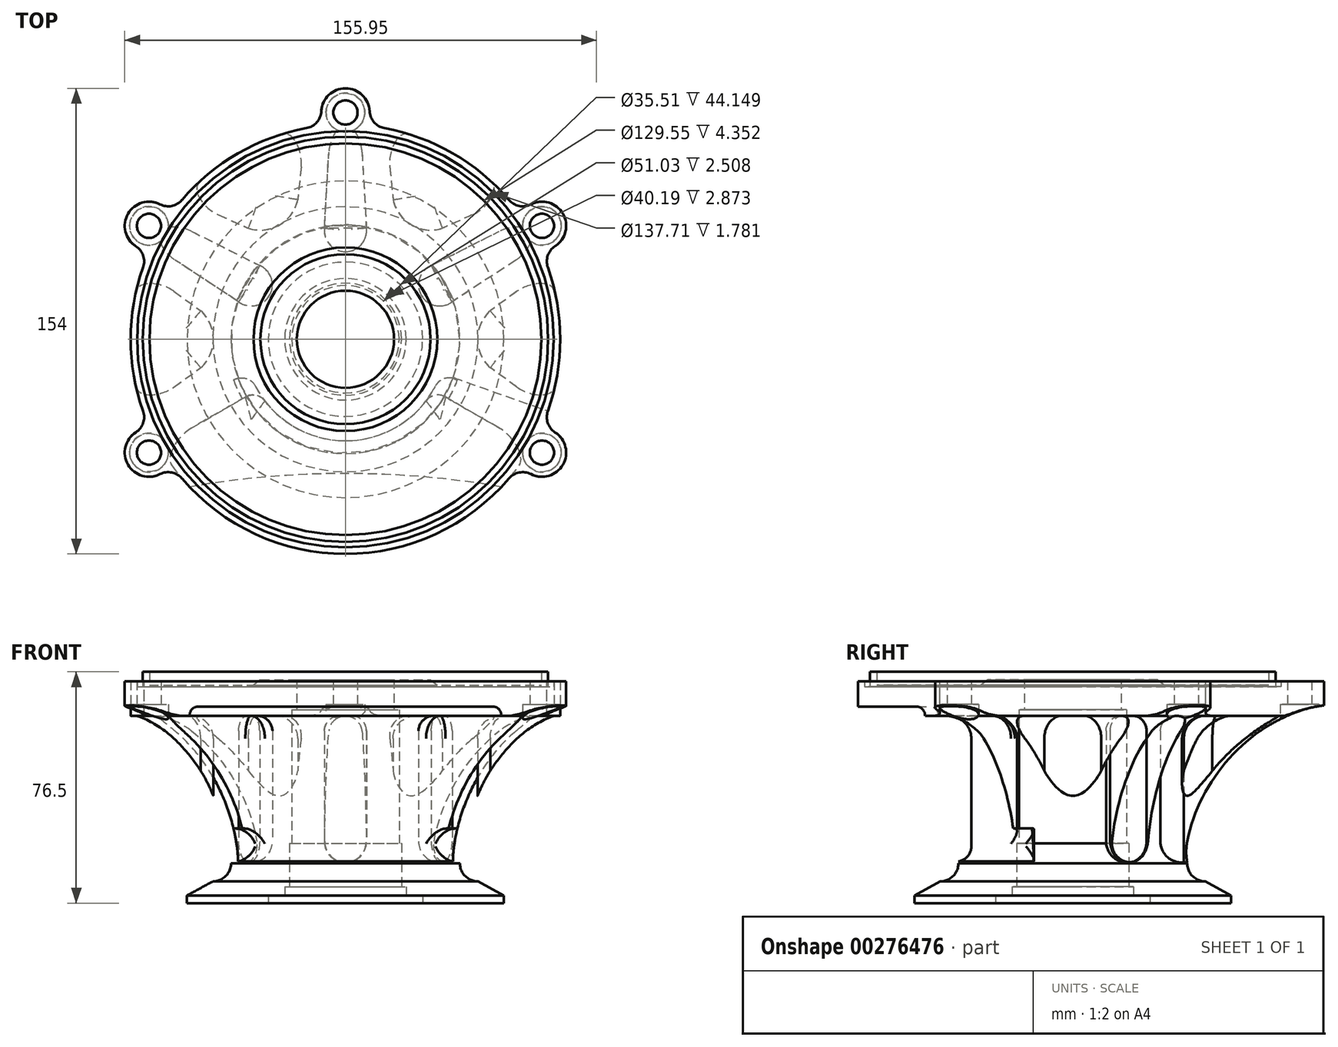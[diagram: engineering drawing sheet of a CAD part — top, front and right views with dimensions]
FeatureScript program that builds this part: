
annotation { "Feature Type Name" : "Feature", "Feature Type Description" : "" }
export const myFeature = defineFeature(function(context is Context, id is Id, definition is map)
    precondition{}
    {
        {
            var Q0;
            Q0=qCreatedBy(makeId("Top.planeOp"),FACE);
            var sketch = newSketch(context, id + "F0", { "sketchPlane" : qUnion([Q0])});
            skCircle(sketch, "E0", {"center": v(0, 0) * mm, "radius": 71 * mm});
            skLineSegment(sketch, "E1", {"start": v(0, 75) * mm, "end": v(0, -75) * mm, "construction": true});
            skCircle(sketch, "E2", {"center": v(0, 0) * mm, "radius": 15 * mm});
            skLineSegment(sketch, "E3", {"start": v(-75, 0) * mm, "end": v(75, 0) * mm, "construction": true});
            skLineSegment(sketch, "E4", {"start": v(-64.95, -37.5) * mm, "end": v(64.95, 37.5) * mm, "construction": true});
            skLineSegment(sketch, "E5.MirrorCS", {"start": v(64.95, -37.5) * mm, "end": v(-64.95, 37.5) * mm, "construction": true});
            skCircle(sketch, "E6", {"center": v(0, 75) * mm, "radius": 4 * mm});
            skCircle(sketch, "E7", {"center": v(-64.95, 37.5) * mm, "radius": 4 * mm});
            skCircle(sketch, "E8", {"center": v(64.95, 37.5) * mm, "radius": 4 * mm});
            skCircle(sketch, "E9", {"center": v(0, 75) * mm, "radius": 8 * mm});
            skCircle(sketch, "E10", {"center": v(64.95, 37.5) * mm, "radius": 8 * mm});
            skCircle(sketch, "E11", {"center": v(-64.95, 37.5) * mm, "radius": 8 * mm});
            skCircle(sketch, "E12", {"center": v(-64.95, -37.5) * mm, "radius": 4 * mm});
            skCircle(sketch, "E13", {"center": v(-64.95, -37.5) * mm, "radius": 8 * mm});
            skCircle(sketch, "E14", {"center": v(64.95, -37.5) * mm, "radius": 4 * mm});
            skCircle(sketch, "E15", {"center": v(64.95, -37.5) * mm, "radius": 8 * mm});
            skSolve(sketch);
        }
        {
            var Q0;
            Q0 = qSketchRegion(id + "F0", true);
            extrude(context, id + "F1", {"entities" : qUnion([Q0]), "depth" : 76.5 * mm});
        }
        {
            var Q0;
            {var subQ0=sQuery(id+"F0.wireOp",EDGE,"Xowyf9vp-Wtrz-lmeA-m8cz-GKDCjoLcK8KI");var subQ1=sQuery(id+"F0.wireOp",EDGE,"E0");Q0=makeQuery(id+"F1.opExtrude","SWEPT_EDGE",EDGE,{"disambiguationData":[OSD([subQ1,subQ0]),TDD([makeQuery(id+"F0.imprint","INTERSECT",VERTEX,{"disambiguationData":[OD(1.0)],"derivedFrom":[subQ1,subQ0]})])]});}
            var Q1;
            {var subQ0=sQuery(id+"F0.wireOp",EDGE,"Xowyf9vp-Wtrz-lmeA-m8cz-GKDCjoLcK8KI");var subQ1=sQuery(id+"F0.wireOp",EDGE,"E0");Q1=makeQuery(id+"F1.opExtrude","SWEPT_EDGE",EDGE,{"disambiguationData":[OSD([subQ1,subQ0]),TDD([makeQuery(id+"F0.imprint","INTERSECT",VERTEX,{"disambiguationData":[OD(0.0)],"derivedFrom":[subQ1,subQ0]})])]});}
            var Q2;
            {var subQ0=sQuery(id+"F0.wireOp",EDGE,"E11");var subQ1=sQuery(id+"F0.wireOp",EDGE,"E0");Q2=makeQuery(id+"F1.opExtrude","SWEPT_EDGE",EDGE,{"disambiguationData":[OSD([subQ1,subQ0]),TDD([makeQuery(id+"F0.imprint","INTERSECT",VERTEX,{"disambiguationData":[OD(0.0)],"derivedFrom":[subQ1,subQ0]})])]});}
            var Q3;
            {var subQ0=sQuery(id+"F0.wireOp",EDGE,"E11");var subQ1=sQuery(id+"F0.wireOp",EDGE,"E0");Q3=makeQuery(id+"F1.opExtrude","SWEPT_EDGE",EDGE,{"disambiguationData":[OSD([subQ1,subQ0]),TDD([makeQuery(id+"F0.imprint","INTERSECT",VERTEX,{"disambiguationData":[OD(1.0)],"derivedFrom":[subQ1,subQ0]})])]});}
            var Q4;
            {var subQ0=sQuery(id+"F0.wireOp",EDGE,"E9");var subQ1=sQuery(id+"F0.wireOp",EDGE,"E0");Q4=makeQuery(id+"F1.opExtrude","SWEPT_EDGE",EDGE,{"disambiguationData":[OSD([subQ1,subQ0]),TDD([makeQuery(id+"F0.imprint","INTERSECT",VERTEX,{"disambiguationData":[OD(1.0)],"derivedFrom":[subQ1,subQ0]})])]});}
            var Q5;
            {var subQ0=sQuery(id+"F0.wireOp",EDGE,"E9");var subQ1=sQuery(id+"F0.wireOp",EDGE,"E0");Q5=makeQuery(id+"F1.opExtrude","SWEPT_EDGE",EDGE,{"disambiguationData":[OSD([subQ1,subQ0]),TDD([makeQuery(id+"F0.imprint","INTERSECT",VERTEX,{"disambiguationData":[OD(0.0)],"derivedFrom":[subQ1,subQ0]})])]});}
            var Q6;
            {var subQ0=sQuery(id+"F0.wireOp",EDGE,"E10");var subQ1=sQuery(id+"F0.wireOp",EDGE,"E0");Q6=makeQuery(id+"F1.opExtrude","SWEPT_EDGE",EDGE,{"disambiguationData":[OSD([subQ1,subQ0]),TDD([makeQuery(id+"F0.imprint","INTERSECT",VERTEX,{"disambiguationData":[OD(1.0)],"derivedFrom":[subQ1,subQ0]})])]});}
            var Q7;
            {var subQ0=sQuery(id+"F0.wireOp",EDGE,"E10");var subQ1=sQuery(id+"F0.wireOp",EDGE,"E0");Q7=makeQuery(id+"F1.opExtrude","SWEPT_EDGE",EDGE,{"disambiguationData":[OSD([subQ1,subQ0]),TDD([makeQuery(id+"F0.imprint","INTERSECT",VERTEX,{"disambiguationData":[OD(0.0)],"derivedFrom":[subQ1,subQ0]})])]});}
            var Q8;
            {var subQ0=sQuery(id+"F0.wireOp",EDGE,"yhjaQ4TD-eABU-w7vi-KoSL-NEqgUzHXku1N");var subQ1=sQuery(id+"F0.wireOp",EDGE,"E0");Q8=makeQuery(id+"F1.opExtrude","SWEPT_EDGE",EDGE,{"disambiguationData":[OSD([subQ1,subQ0]),TDD([makeQuery(id+"F0.imprint","INTERSECT",VERTEX,{"disambiguationData":[OD(0.0)],"derivedFrom":[subQ1,subQ0]})])]});}
            var Q9;
            {var subQ0=sQuery(id+"F0.wireOp",EDGE,"yhjaQ4TD-eABU-w7vi-KoSL-NEqgUzHXku1N");var subQ1=sQuery(id+"F0.wireOp",EDGE,"E0");Q9=makeQuery(id+"F1.opExtrude","SWEPT_EDGE",EDGE,{"disambiguationData":[OSD([subQ1,subQ0]),TDD([makeQuery(id+"F0.imprint","INTERSECT",VERTEX,{"disambiguationData":[OD(1.0)],"derivedFrom":[subQ1,subQ0]})])]});}
            var Q10;
            {var subQ0=sQuery(id+"F0.wireOp",EDGE,"E13");var subQ1=sQuery(id+"F0.wireOp",EDGE,"E0");Q10=makeQuery(id+"F1.opExtrude","SWEPT_EDGE",EDGE,{"disambiguationData":[OSD([subQ1,subQ0]),TDD([makeQuery(id+"F0.imprint","INTERSECT",VERTEX,{"disambiguationData":[OD(0.0)],"derivedFrom":[subQ1,subQ0]})])]});}
            var Q11;
            {var subQ0=sQuery(id+"F0.wireOp",EDGE,"E13");var subQ1=sQuery(id+"F0.wireOp",EDGE,"E0");Q11=makeQuery(id+"F1.opExtrude","SWEPT_EDGE",EDGE,{"disambiguationData":[OSD([subQ1,subQ0]),TDD([makeQuery(id+"F0.imprint","INTERSECT",VERTEX,{"disambiguationData":[OD(1.0)],"derivedFrom":[subQ1,subQ0]})])]});}
            var Q12;
            {var subQ0=sQuery(id+"F0.wireOp",EDGE,"E15");var subQ1=sQuery(id+"F0.wireOp",EDGE,"E0");Q12=makeQuery(id+"F1.opExtrude","SWEPT_EDGE",EDGE,{"disambiguationData":[OSD([subQ1,subQ0]),TDD([makeQuery(id+"F0.imprint","INTERSECT",VERTEX,{"disambiguationData":[OD(0.0)],"derivedFrom":[subQ1,subQ0]})])]});}
            var Q13;
            {var subQ0=sQuery(id+"F0.wireOp",EDGE,"E15");var subQ1=sQuery(id+"F0.wireOp",EDGE,"E0");Q13=makeQuery(id+"F1.opExtrude","SWEPT_EDGE",EDGE,{"disambiguationData":[OSD([subQ1,subQ0]),TDD([makeQuery(id+"F0.imprint","INTERSECT",VERTEX,{"disambiguationData":[OD(1.0)],"derivedFrom":[subQ1,subQ0]})])]});}
            fillet(context, id + "F2", {"entities" : qUnion([Q0, Q1, Q2, Q3, Q4, Q5, Q6, Q7, Q8, Q9, Q10, Q11, Q12, Q13]), "radius" : 6 * mm, "tangentPropagation" : true, "allowEdgeOverflow" : false});
        }
        {
            var Q0;
            Q0=qCreatedBy(makeId("Front.planeOp"),FACE);
            var sketch = newSketch(context, id + "F3", { "sketchPlane" : qUnion([Q0])});
            skLineSegment(sketch, "E16", {"start": v(0, 91.9) * mm, "end": v(98, 91.9) * mm});
            skLineSegment(sketch, "E17", {"start": v(0, 91.9) * mm, "end": v(0, 0) * mm});
            skLineSegment(sketch, "E18", {"start": v(0, 0) * mm, "end": v(0, -15.6) * mm});
            skLineSegment(sketch, "E19", {"start": v(98, 91.9) * mm, "end": v(98, 73.4) * mm});
            skLineSegment(sketch, "E20", {"start": v(98, 73.4) * mm, "end": v(68.85, 73.4) * mm});
            skLineSegment(sketch, "E21", {"start": v(68.85, 73.4) * mm, "end": v(68.85, 71.6) * mm});
            skLineSegment(sketch, "E22", {"start": v(68.85, 71.6) * mm, "end": v(67, 71.6) * mm});
            skLineSegment(sketch, "E23", {"start": v(67, 71.6) * mm, "end": v(67, 76.5) * mm});
            skLineSegment(sketch, "E24", {"start": v(67, 76.5) * mm, "end": v(64.78, 76.5) * mm});
            skLineSegment(sketch, "E25", {"start": v(64.78, 76.5) * mm, "end": v(64.78, 72.15) * mm});
            skLineSegment(sketch, "E26", {"start": v(64.78, 72.15) * mm, "end": v(30.38, 72.15) * mm});
            skLineSegment(sketch, "E27", {"start": v(28.11, 73.9) * mm, "end": v(16.06, 73.9) * mm});
            skLineSegment(sketch, "E28", {"start": v(16.06, 73.9) * mm, "end": v(16.06, 63.9) * mm});
            skLineSegment(sketch, "E29", {"start": v(16.06, 63.9) * mm, "end": v(17.76, 63.9) * mm});
            skLineSegment(sketch, "E30", {"start": v(0, -15.6) * mm, "end": v(98, -15.6) * mm});
            skLineSegment(sketch, "E31", {"start": v(98, -15.6) * mm, "end": v(98, 65.9) * mm});
            skLineSegment(sketch, "E32", {"start": v(17.76, 63.9) * mm, "end": v(17.76, 19.75) * mm});
            skLineSegment(sketch, "E33", {"start": v(17.76, 19.75) * mm, "end": v(18.54, 19.75) * mm});
            skLineSegment(sketch, "E34", {"start": v(18.54, 19.75) * mm, "end": v(18.54, 5.38) * mm});
            skLineSegment(sketch, "E35", {"start": v(18.54, 5.38) * mm, "end": v(20.1, 5.38) * mm});
            skLineSegment(sketch, "E36", {"start": v(20.1, 5.38) * mm, "end": v(20.1, 2.5) * mm});
            skLineSegment(sketch, "E37", {"start": v(20.1, 2.5) * mm, "end": v(25.52, 2.5) * mm});
            skLineSegment(sketch, "E38", {"start": v(25.52, 2.5) * mm, "end": v(25.52, 0) * mm});
            skLineSegment(sketch, "E39", {"start": v(25.52, 0) * mm, "end": v(52.38, 0) * mm});
            skLineSegment(sketch, "E40", {"start": v(52.38, 0) * mm, "end": v(52.38, 2.5) * mm});
            skLineSegment(sketch, "E41", {"start": v(52.38, 2.5) * mm, "end": v(43.83, 7.18) * mm});
            skLineSegment(sketch, "E42", {"start": v(43.83, 7.18) * mm, "end": v(43.81, 7.18) * mm});
            skLineSegment(sketch, "E43", {"start": v(98, 65.9) * mm, "end": v(87.97, 65.9) * mm});
            skPoint(sketch, "E44.visualSharp", {"position": v(37.81, 7.18) * mm});
            skArc(sketch, "E44.filletArc", {"start": v(37.81, 13.18) * mm, "mid": v(39.57, 8.94) * mm, "end": v(43.81, 7.18) * mm});
            skFitSpline(sketch, "E45", {"points": [v(37.81, 13.18) * mm, v(87.97, 65.9) * mm], "startDerivative": vector(-0.87, 63.39) * mm, "endDerivative": vector(91.68, 3.94) * mm});
            skLineSegment(sketch, "E46", {"start": v(25.52, 0) * mm, "end": v(0, 0) * mm, "construction": true});
            skLineSegment(sketch, "E47", {"start": v(28.11, 73.9) * mm, "end": v(30.38, 72.15) * mm});
            skSolve(sketch);
        }
        {
            var Q0;
            Q0 = qSketchRegion(id + "F3", true);
            var Q1;
            Q1=sQuery(id+"F3.wireOp",EDGE,"E17");
            revolve(context, id + "F4", {"operationType" : NewBodyOperationType.REMOVE, "entities" : qUnion([Q0]), "axis" : qUnion([Q1]), "revolveType" : RevolveType.FULL, "oppositeDirection" : true});
        }
        {
            var Q0;
            Q0=qCreatedBy(makeId("Top.planeOp"),FACE);
            var sketch = newSketch(context, id + "F5", { "sketchPlane" : qUnion([Q0])});
            skCircle(sketch, "E48", {"center": v(0, 0) * mm, "radius": 43.67 * mm, "construction": true});
            skLineSegment(sketch, "E49", {"start": v(88.93, -51.34) * mm, "end": v(-88.93, 51.34) * mm, "construction": true});
            skLineSegment(sketch, "E50", {"start": v(-118.94, 0) * mm, "end": v(121.39, 0) * mm, "construction": true});
            skLineSegment(sketch, "E51", {"start": v(0, -76.85) * mm, "end": v(0, 108.09) * mm, "construction": true});
            skLineSegment(sketch, "E52.MirrorCS", {"start": v(-88.93, -51.34) * mm, "end": v(88.93, 51.34) * mm, "construction": true});
            skArc(sketch, "E53", {"start": v(4.56, 78.17) * mm, "mid": v(0, 82.73) * mm, "end": v(-4.56, 78.17) * mm});
            skArc(sketch, "E54", {"start": v(-6.93, 36.75) * mm, "mid": v(0, 28.98) * mm, "end": v(6.93, 36.75) * mm});
            skLineSegment(sketch, "E55", {"start": v(-6.98, 35.95) * mm, "end": v(6.98, 35.95) * mm, "construction": true});
            skLineSegment(sketch, "E56", {"start": v(-4.56, 78.17) * mm, "end": v(4.56, 78.17) * mm, "construction": true});
            skLineSegment(sketch, "E57", {"start": v(4.56, 78.17) * mm, "end": v(6.98, 35.95) * mm});
            skLineSegment(sketch, "E58", {"start": v(-6.98, 35.95) * mm, "end": v(-4.56, 78.17) * mm});
            skArc(sketch, "E59.1.0", {"start": v(28.36, 24.38) * mm, "mid": v(25.1, 14.49) * mm, "end": v(35.3, 12.37) * mm});
            skLineSegment(sketch, "E59.1.1", {"start": v(27.65, 24.02) * mm, "end": v(65.42, 43.03) * mm});
            skLineSegment(sketch, "E59.1.2", {"start": v(69.98, 35.14) * mm, "end": v(34.63, 11.93) * mm});
            skArc(sketch, "E59.1.3", {"start": v(69.98, 35.14) * mm, "mid": v(71.65, 41.36) * mm, "end": v(65.42, 43.03) * mm});
            skLineSegment(sketch, "E59.anchor1", {"start": v(0, 0) * mm, "end": v(-6.93, 36.75) * mm, "construction": true});
            skLineSegment(sketch, "E59.anchor2", {"start": v(0, 0) * mm, "end": v(28.36, 24.38) * mm, "construction": true});
            skLineSegment(sketch, "E60.anchor2", {"start": v(0, 0) * mm, "end": v(6.93, -36.75) * mm, "construction": true});
            skLineSegment(sketch, "E61.1.0", {"start": v(-65.42, 43.03) * mm, "end": v(-27.65, 24.02) * mm});
            skArc(sketch, "E61.1.1", {"start": v(-65.42, 43.03) * mm, "mid": v(-71.65, 41.36) * mm, "end": v(-69.98, 35.14) * mm});
            skLineSegment(sketch, "E61.1.2", {"start": v(-34.63, 11.93) * mm, "end": v(-69.98, 35.14) * mm});
            skArc(sketch, "E61.1.3", {"start": v(-35.3, 12.37) * mm, "mid": v(-25.1, 14.49) * mm, "end": v(-28.36, 24.38) * mm});
            skLineSegment(sketch, "E61.anchor1", {"start": v(0, 0) * mm, "end": v(-4.56, -78.17) * mm, "construction": true});
            skLineSegment(sketch, "E61.anchor2", {"start": v(0, 0) * mm, "end": v(-65.42, 43.03) * mm, "construction": true});
            skArc(sketch, "E62", {"start": v(-101.6, 0) * mm, "mid": v(-90.55, -20.82) * mm, "end": v(-67.1, -23.33) * mm});
            skLineSegment(sketch, "E63", {"start": v(-67.1, -23.33) * mm, "end": v(-47.84, -9.43) * mm});
            skArc(sketch, "E64.trimOffspring", {"start": v(-47.84, -9.43) * mm, "mid": v(-44.76, -5.15) * mm, "end": v(-43.67, 0) * mm});
            skArc(sketch, "E65.MirrorCS", {"start": v(-101.6, 0) * mm, "mid": v(-90.55, 20.82) * mm, "end": v(-67.1, 23.33) * mm});
            skLineSegment(sketch, "E66.MirrorCS", {"start": v(-67.1, 23.33) * mm, "end": v(-47.84, 9.43) * mm});
            skArc(sketch, "E67.MirrorCS", {"start": v(-47.84, 9.43) * mm, "mid": v(-44.76, 5.15) * mm, "end": v(-43.67, 0) * mm});
            skArc(sketch, "E68.1.0", {"start": v(-50.8, 88) * mm, "mid": v(-63.3, 68) * mm, "end": v(-53.76, 46.45) * mm});
            skLineSegment(sketch, "E68.1.1", {"start": v(-53.76, 46.45) * mm, "end": v(-32.08, 36.71) * mm});
            skArc(sketch, "E68.1.2", {"start": v(-32.08, 36.71) * mm, "mid": v(-26.84, 36.18) * mm, "end": v(-21.83, 37.82) * mm});
            skArc(sketch, "E68.1.3", {"start": v(-15.75, 46.14) * mm, "mid": v(-17.92, 41.34) * mm, "end": v(-21.83, 37.82) * mm});
            skLineSegment(sketch, "E68.1.4", {"start": v(-13.35, 69.78) * mm, "end": v(-15.75, 46.14) * mm});
            skArc(sketch, "E68.1.5", {"start": v(-50.8, 88) * mm, "mid": v(-27.24, 88.83) * mm, "end": v(-13.35, 69.78) * mm});
            skArc(sketch, "E68.2.0", {"start": v(50.8, 88) * mm, "mid": v(27.24, 88.83) * mm, "end": v(13.35, 69.78) * mm});
            skLineSegment(sketch, "E68.2.1", {"start": v(13.35, 69.78) * mm, "end": v(15.75, 46.14) * mm});
            skArc(sketch, "E68.2.2", {"start": v(15.75, 46.14) * mm, "mid": v(17.92, 41.34) * mm, "end": v(21.83, 37.82) * mm});
            skArc(sketch, "E68.2.3", {"start": v(32.08, 36.71) * mm, "mid": v(26.84, 36.18) * mm, "end": v(21.83, 37.82) * mm});
            skLineSegment(sketch, "E68.2.4", {"start": v(53.76, 46.45) * mm, "end": v(32.08, 36.71) * mm});
            skArc(sketch, "E68.2.5", {"start": v(50.8, 88) * mm, "mid": v(63.3, 68) * mm, "end": v(53.76, 46.45) * mm});
            skArc(sketch, "E68.3.0", {"start": v(101.6, 0) * mm, "mid": v(90.55, 20.82) * mm, "end": v(67.1, 23.33) * mm});
            skLineSegment(sketch, "E68.3.1", {"start": v(67.1, 23.33) * mm, "end": v(47.84, 9.43) * mm});
            skArc(sketch, "E68.3.2", {"start": v(47.84, 9.43) * mm, "mid": v(44.76, 5.15) * mm, "end": v(43.67, 0) * mm});
            skArc(sketch, "E68.3.3", {"start": v(47.84, -9.43) * mm, "mid": v(44.76, -5.15) * mm, "end": v(43.67, 0) * mm});
            skLineSegment(sketch, "E68.3.4", {"start": v(67.1, -23.33) * mm, "end": v(47.84, -9.43) * mm});
            skArc(sketch, "E68.3.5", {"start": v(101.6, 0) * mm, "mid": v(90.55, -20.82) * mm, "end": v(67.1, -23.33) * mm});
            skLineSegment(sketch, "E68.anchor1", {"start": v(0, 0) * mm, "end": v(-101.6, 0) * mm, "construction": true});
            skLineSegment(sketch, "E68.anchor2", {"start": v(0, 0) * mm, "end": v(101.6, 0) * mm, "construction": true});
            skCircle(sketch, "E69.0", {"center": v(-64.95, -37.5) * mm, "radius": 4 * mm});
            skCircle(sketch, "E70.0", {"center": v(64.95, -37.5) * mm, "radius": 4 * mm});
            skLineSegment(sketch, "E71", {"start": v(-64.95, -37.5) * mm, "end": v(-29.05, -16.77) * mm});
            skLineSegment(sketch, "E72", {"start": v(64.95, -37.5) * mm, "end": v(29.05, -16.77) * mm});
            skArc(sketch, "E73", {"start": v(-63.86, -47.91) * mm, "mid": v(0, -79.83) * mm, "end": v(63.86, -47.91) * mm});
            skArc(sketch, "E74", {"start": v(63.86, -47.91) * mm, "mid": v(65.4, -41.07) * mm, "end": v(61.3, -35.4) * mm});
            skArc(sketch, "E75.MirrorC", {"start": v(-63.86, -47.91) * mm, "mid": v(-65.4, -41.07) * mm, "end": v(-61.3, -35.4) * mm});
            skArc(sketch, "E76.trimOffspring", {"start": v(-29.05, -16.77) * mm, "mid": v(0, -33.55) * mm, "end": v(29.05, -16.77) * mm});
            skArc(sketch, "E77.trimOffspring", {"start": v(-6.22, 32.97) * mm, "mid": v(-6.26, 32.96) * mm, "end": v(-6.3, 32.95) * mm});
            skArc(sketch, "E78.trimOffspring", {"start": v(25.44, 21.87) * mm, "mid": v(25.41, 21.9) * mm, "end": v(25.39, 21.93) * mm});
            skSolve(sketch);
        }
        {
            var Q0;
            Q0 = qSketchRegion(id + "F5", true);
            extrude(context, id + "F6", {"entities" : qUnion([Q0]), "operationType" : NewBodyOperationType.REMOVE, "depth" : 61.94 * mm, "hasSecondDirection" : true, "secondDirectionOppositeDirection" : false, "secondDirectionDepth" : 20.4 * mm});
        }
        {
            var Q0;
            Q0=makeQuery(id+"F6.boolean.opBoolean","COPY",FACE,{"derivedFrom":makeQuery(id+"F6.opExtrude","CAP_FACE",FACE,{"disambiguationData":[OSD([sQuery(id+"F5.wireOp",EDGE,"E59.1.0"),sQuery(id+"F5.wireOp",EDGE,"E59.1.1"),sQuery(id+"F5.wireOp",EDGE,"E59.1.2"),sQuery(id+"F5.wireOp",EDGE,"E59.1.3")])],"isStart":true})});
            var sketch = newSketch(context, id + "F7", { "sketchPlane" : qUnion([Q0])});
            skLineSegment(sketch, "E79.0.0", {"start": v(29.31, 24.86) * mm, "end": v(28.36, 24.38) * mm});
            skArc(sketch, "E79.0.1", {"start": v(28.36, 24.38) * mm, "mid": v(25.1, 14.49) * mm, "end": v(35.3, 12.37) * mm});
            skLineSegment(sketch, "E79.0.2", {"start": v(35.3, 12.37) * mm, "end": v(36.18, 12.96) * mm});
            skArc(sketch, "E79.0.3", {"start": v(36.18, 12.96) * mm, "mid": v(33.28, 19.22) * mm, "end": v(29.31, 24.86) * mm});
            skLineSegment(sketch, "E80", {"start": v(31.14, 17.98) * mm, "end": v(33.28, 19.22) * mm});
            skLineSegment(sketch, "E81", {"start": v(33.28, 19.22) * mm, "end": v(25.1, 14.49) * mm});
            skSolve(sketch);
        }
        {
            var Q0;
            {var subQ1=sQuery(id+"F7.wireOp",EDGE,"E79.0.0");Q0=makeQuery(id+"F7.imprint","IMPRINT",FACE,{"disambiguationData":[TD([[makeQuery(id+"F7.imprint","IMPRINT",EDGE,{"derivedFrom":subQ1}),-1.0]])]});}
            var Q1;
            Q1=sQuery(id+"F7.wireOp",EDGE,"E81");
            revolve(context, id + "F8", {"operationType" : NewBodyOperationType.REMOVE, "entities" : qUnion([Q0]), "axis" : qUnion([Q1]), "revolveType" : RevolveType.FULL, "oppositeDirection" : true});
        }
        {
            var Q0;
            Q0=makeQuery(id+"F6.boolean.opBoolean","COPY",FACE,{"derivedFrom":makeQuery(id+"F6.opExtrude","CAP_FACE",FACE,{"disambiguationData":[OSD([sQuery(id+"F5.wireOp",EDGE,"E53"),sQuery(id+"F5.wireOp",EDGE,"E54"),sQuery(id+"F5.wireOp",EDGE,"E57"),sQuery(id+"F5.wireOp",EDGE,"E58")])],"isStart":true})});
            var sketch = newSketch(context, id + "F9", { "sketchPlane" : qUnion([Q0])});
            skLineSegment(sketch, "E82.0.0", {"start": v(-6.87, 37.81) * mm, "end": v(-6.93, 36.75) * mm});
            skArc(sketch, "E82.0.1", {"start": v(-6.93, 36.75) * mm, "mid": v(0, 28.98) * mm, "end": v(6.93, 36.75) * mm});
            skLineSegment(sketch, "E82.0.2", {"start": v(6.93, 36.75) * mm, "end": v(6.87, 37.81) * mm});
            skArc(sketch, "E82.0.3", {"start": v(6.87, 37.81) * mm, "mid": v(0, 38.43) * mm, "end": v(-6.87, 37.81) * mm});
            skLineSegment(sketch, "E83", {"start": v(0, 28.98) * mm, "end": v(0, 38.43) * mm});
            skSolve(sketch);
        }
        {
            var Q0;
            {var subQ0=sQuery(id+"F9.wireOp",EDGE,"E82.0.0");Q0=makeQuery(id+"F9.imprint","IMPRINT",FACE,{"disambiguationData":[TD([[makeQuery(id+"F9.imprint","IMPRINT",EDGE,{"derivedFrom":subQ0}),-1.0]])]});}
            var Q1;
            Q1=sQuery(id+"F9.wireOp",EDGE,"E83");
            revolve(context, id + "F10", {"operationType" : NewBodyOperationType.REMOVE, "entities" : qUnion([Q0]), "axis" : qUnion([Q1]), "revolveType" : RevolveType.FULL, "oppositeDirection" : true});
        }
        {
            var Q0;
            Q0=makeQuery(id+"F6.boolean.opBoolean","COPY",FACE,{"derivedFrom":makeQuery(id+"F6.opExtrude","CAP_FACE",FACE,{"disambiguationData":[OSD([sQuery(id+"F5.wireOp",EDGE,"E61.1.0"),sQuery(id+"F5.wireOp",EDGE,"E61.1.1"),sQuery(id+"F5.wireOp",EDGE,"E61.1.2"),sQuery(id+"F5.wireOp",EDGE,"E61.1.3")])],"isStart":true})});
            var sketch = newSketch(context, id + "F11", { "sketchPlane" : qUnion([Q0])});
            skLineSegment(sketch, "E84.0.0", {"start": v(-36.18, 12.96) * mm, "end": v(-35.3, 12.37) * mm});
            skArc(sketch, "E84.0.1", {"start": v(-35.3, 12.37) * mm, "mid": v(-25.1, 14.49) * mm, "end": v(-28.36, 24.38) * mm});
            skLineSegment(sketch, "E84.0.2", {"start": v(-28.36, 24.38) * mm, "end": v(-29.31, 24.86) * mm});
            skArc(sketch, "E84.0.3", {"start": v(-29.31, 24.86) * mm, "mid": v(-33.28, 19.22) * mm, "end": v(-36.18, 12.96) * mm});
            skLineSegment(sketch, "E85", {"start": v(-25.1, 14.49) * mm, "end": v(-33.28, 19.22) * mm});
            skSolve(sketch);
        }
        {
            var Q0;
            {var subQ0=sQuery(id+"F11.wireOp",EDGE,"E84.0.0");Q0=makeQuery(id+"F11.imprint","IMPRINT",FACE,{"disambiguationData":[TD([[makeQuery(id+"F11.imprint","IMPRINT",EDGE,{"derivedFrom":subQ0}),-1.0]])]});}
            var Q1;
            Q1=sQuery(id+"F11.wireOp",EDGE,"E85");
            revolve(context, id + "F12", {"operationType" : NewBodyOperationType.REMOVE, "entities" : qUnion([Q0]), "axis" : qUnion([Q1]), "revolveType" : RevolveType.FULL, "oppositeDirection" : true});
        }
        {
            var Q0;
            Q0=makeQuery(id+"F6.boolean.opBoolean","COPY",EDGE,{"derivedFrom":makeQuery(id+"F6.opExtrude","CAP_EDGE",EDGE,{"disambiguationData":[OSD([sQuery(id+"F5.wireOp",EDGE,"E68.1.2"),sQuery(id+"F5.wireOp",EDGE,"E68.1.3")])],"isStart":false})});
            var Q1;
            Q1=makeQuery(id+"F6.boolean.opBoolean","COPY",EDGE,{"derivedFrom":makeQuery(id+"F6.opExtrude","CAP_EDGE",EDGE,{"disambiguationData":[OSD([sQuery(id+"F5.wireOp",EDGE,"E68.1.1")])],"isStart":false})});
            var Q2;
            Q2=makeQuery(id+"F6.boolean.opBoolean","COPY",EDGE,{"derivedFrom":makeQuery(id+"F6.opExtrude","CAP_EDGE",EDGE,{"disambiguationData":[OSD([sQuery(id+"F5.wireOp",EDGE,"E68.1.4")])],"isStart":false})});
            var Q3;
            Q3=makeQuery(id+"F6.boolean.opBoolean","COPY",EDGE,{"derivedFrom":makeQuery(id+"F6.opExtrude","CAP_EDGE",EDGE,{"disambiguationData":[OSD([sQuery(id+"F5.wireOp",EDGE,"E68.2.1")])],"isStart":false})});
            var Q4;
            Q4=makeQuery(id+"F6.boolean.opBoolean","COPY",EDGE,{"derivedFrom":makeQuery(id+"F6.opExtrude","CAP_EDGE",EDGE,{"disambiguationData":[OSD([sQuery(id+"F5.wireOp",EDGE,"E68.2.2"),sQuery(id+"F5.wireOp",EDGE,"E68.2.3")])],"isStart":false})});
            var Q5;
            Q5=makeQuery(id+"F6.boolean.opBoolean","COPY",EDGE,{"derivedFrom":makeQuery(id+"F6.opExtrude","CAP_EDGE",EDGE,{"disambiguationData":[OSD([sQuery(id+"F5.wireOp",EDGE,"E68.2.4")])],"isStart":false})});
            var Q6;
            Q6=makeQuery(id+"F6.boolean.opBoolean","COPY",EDGE,{"derivedFrom":makeQuery(id+"F6.opExtrude","CAP_EDGE",EDGE,{"disambiguationData":[OSD([sQuery(id+"F5.wireOp",EDGE,"E68.3.1")])],"isStart":false})});
            var Q7;
            Q7=makeQuery(id+"F6.boolean.opBoolean","COPY",EDGE,{"derivedFrom":makeQuery(id+"F6.opExtrude","CAP_EDGE",EDGE,{"disambiguationData":[OSD([sQuery(id+"F5.wireOp",EDGE,"E68.3.2"),sQuery(id+"F5.wireOp",EDGE,"E68.3.3")])],"isStart":false})});
            var Q8;
            Q8=makeQuery(id+"F6.boolean.opBoolean","COPY",EDGE,{"derivedFrom":makeQuery(id+"F6.opExtrude","CAP_EDGE",EDGE,{"disambiguationData":[OSD([sQuery(id+"F5.wireOp",EDGE,"E68.3.4")])],"isStart":false})});
            var Q9;
            Q9=makeQuery(id+"F6.boolean.opBoolean","COPY",EDGE,{"derivedFrom":makeQuery(id+"F6.opExtrude","CAP_EDGE",EDGE,{"disambiguationData":[OSD([sQuery(id+"F5.wireOp",EDGE,"E72")])],"isStart":false})});
            var Q10;
            Q10=makeQuery(id+"F6.boolean.opBoolean","COPY",EDGE,{"derivedFrom":makeQuery(id+"F6.opExtrude","CAP_EDGE",EDGE,{"disambiguationData":[OSD([sQuery(id+"F5.wireOp",EDGE,"E76.trimOffspring")])],"isStart":false})});
            var Q11;
            Q11=makeQuery(id+"F6.boolean.opBoolean","COPY",EDGE,{"derivedFrom":makeQuery(id+"F6.opExtrude","CAP_EDGE",EDGE,{"disambiguationData":[OSD([sQuery(id+"F5.wireOp",EDGE,"E71")])],"isStart":false})});
            var Q12;
            Q12=makeQuery(id+"F6.boolean.opBoolean","COPY",EDGE,{"derivedFrom":makeQuery(id+"F6.opExtrude","CAP_EDGE",EDGE,{"disambiguationData":[OSD([sQuery(id+"F5.wireOp",EDGE,"E64.trimOffspring"),sQuery(id+"F5.wireOp",EDGE,"E67.MirrorCS")])],"isStart":false})});
            var Q13;
            Q13=makeQuery(id+"F6.boolean.opBoolean","COPY",EDGE,{"derivedFrom":makeQuery(id+"F6.opExtrude","CAP_EDGE",EDGE,{"disambiguationData":[OSD([sQuery(id+"F5.wireOp",EDGE,"E63")])],"isStart":false})});
            var Q14;
            Q14=makeQuery(id+"F6.boolean.opBoolean","COPY",EDGE,{"derivedFrom":makeQuery(id+"F6.opExtrude","CAP_EDGE",EDGE,{"disambiguationData":[OSD([sQuery(id+"F5.wireOp",EDGE,"E66.MirrorCS")])],"isStart":false})});
            fillet(context, id + "F13", {"entities" : qUnion([Q0, Q1, Q2, Q3, Q4, Q5, Q6, Q7, Q8, Q9, Q10, Q11, Q12, Q13, Q14]), "radius" : 7.5 * mm, "tangentPropagation" : true, "allowEdgeOverflow" : false});
        }
        {
            var Q0;
            Q0=makeQuery(id+"F6.boolean.opBoolean","COPY",EDGE,{"derivedFrom":makeQuery(id+"F6.opExtrude","CAP_EDGE",EDGE,{"disambiguationData":[OSD([sQuery(id+"F5.wireOp",EDGE,"E54")])],"isStart":false})});
            var Q1;
            Q1=makeQuery(id+"F6.boolean.opBoolean","COPY",EDGE,{"derivedFrom":makeQuery(id+"F6.opExtrude","CAP_EDGE",EDGE,{"disambiguationData":[OSD([sQuery(id+"F5.wireOp",EDGE,"E58")])],"isStart":false})});
            var Q2;
            Q2=makeQuery(id+"F6.boolean.opBoolean","COPY",EDGE,{"derivedFrom":makeQuery(id+"F6.opExtrude","CAP_EDGE",EDGE,{"disambiguationData":[OSD([sQuery(id+"F5.wireOp",EDGE,"E57")])],"isStart":false})});
            var Q3;
            Q3=makeQuery(id+"F6.boolean.opBoolean","COPY",EDGE,{"derivedFrom":makeQuery(id+"F6.opExtrude","CAP_EDGE",EDGE,{"disambiguationData":[OSD([sQuery(id+"F5.wireOp",EDGE,"E59.1.0")])],"isStart":false})});
            var Q4;
            Q4=makeQuery(id+"F6.boolean.opBoolean","COPY",EDGE,{"derivedFrom":makeQuery(id+"F6.opExtrude","CAP_EDGE",EDGE,{"disambiguationData":[OSD([sQuery(id+"F5.wireOp",EDGE,"E59.1.1")])],"isStart":false})});
            var Q5;
            Q5=makeQuery(id+"F6.boolean.opBoolean","COPY",EDGE,{"derivedFrom":makeQuery(id+"F6.opExtrude","CAP_EDGE",EDGE,{"disambiguationData":[OSD([sQuery(id+"F5.wireOp",EDGE,"E59.1.2")])],"isStart":false})});
            var Q6;
            Q6=makeQuery(id+"F6.boolean.opBoolean","COPY",EDGE,{"derivedFrom":makeQuery(id+"F6.opExtrude","CAP_EDGE",EDGE,{"disambiguationData":[OSD([sQuery(id+"F5.wireOp",EDGE,"E61.1.3")])],"isStart":false})});
            var Q7;
            Q7=makeQuery(id+"F6.boolean.opBoolean","COPY",EDGE,{"derivedFrom":makeQuery(id+"F6.opExtrude","CAP_EDGE",EDGE,{"disambiguationData":[OSD([sQuery(id+"F5.wireOp",EDGE,"E61.1.2")])],"isStart":false})});
            var Q8;
            Q8=makeQuery(id+"F6.boolean.opBoolean","COPY",EDGE,{"derivedFrom":makeQuery(id+"F6.opExtrude","CAP_EDGE",EDGE,{"disambiguationData":[OSD([sQuery(id+"F5.wireOp",EDGE,"E61.1.0")])],"isStart":false})});
            fillet(context, id + "F14", {"entities" : qUnion([Q0, Q1, Q2, Q3, Q4, Q5, Q6, Q7, Q8]), "radius" : 5 * mm, "tangentPropagation" : true, "allowEdgeOverflow" : false});
        }
        {
            var Q0;
            Q0=makeQuery(id+"F6.boolean.opBoolean","COPY",FACE,{"derivedFrom":makeQuery(id+"F6.opExtrude","CAP_FACE",FACE,{"disambiguationData":[OSD([sQuery(id+"F5.wireOp",EDGE,"E69.0"),sQuery(id+"F5.wireOp",EDGE,"E70.0"),sQuery(id+"F5.wireOp",EDGE,"E71"),sQuery(id+"F5.wireOp",EDGE,"E72"),sQuery(id+"F5.wireOp",EDGE,"E73"),sQuery(id+"F5.wireOp",EDGE,"E74"),sQuery(id+"F5.wireOp",EDGE,"E75.MirrorC"),sQuery(id+"F5.wireOp",EDGE,"E76.trimOffspring")])],"isStart":false})});
            var sketch = newSketch(context, id + "F15", { "sketchPlane" : qUnion([Q0])});
            skLineSegment(sketch, "E86", {"start": v(0, 42.72) * mm, "end": v(0, 193.24) * mm, "construction": true});
            skCircle(sketch, "E87", {"center": v(0, 346.97) * mm, "radius": 302.56 * mm});
            skSolve(sketch);
        }
        {
            var Q0;
            Q0 = qSketchRegion(id + "F15", true);
            extrude(context, id + "F16", {"entities" : qUnion([Q0]), "operationType" : NewBodyOperationType.REMOVE, "oppositeDirection" : true, "depth" : 3 * mm});
        }
        {
            var Q0;
            Q0=makeQuery(id+"F16.boolean.opBoolean","COPY",EDGE,{"derivedFrom":makeQuery(id+"F16.opExtrude","CAP_EDGE",EDGE,{"disambiguationData":[OSD([sQuery(id+"F15.wireOp",EDGE,"E87")])],"isStart":false})});
            fillet(context, id + "F17", {"entities" : qUnion([Q0]), "radius" : 3 * mm, "tangentPropagation" : true, "allowEdgeOverflow" : false});
        }
        {
            var Q0;
            Q0=makeQuery(id+"F6.boolean.opBoolean","COPY",FACE,{"derivedFrom":makeQuery(id+"F6.opExtrude","CAP_FACE",FACE,{"disambiguationData":[OSD([sQuery(id+"F5.wireOp",EDGE,"E69.0"),sQuery(id+"F5.wireOp",EDGE,"E70.0"),sQuery(id+"F5.wireOp",EDGE,"E71"),sQuery(id+"F5.wireOp",EDGE,"E72"),sQuery(id+"F5.wireOp",EDGE,"E73"),sQuery(id+"F5.wireOp",EDGE,"E74"),sQuery(id+"F5.wireOp",EDGE,"E75.MirrorC"),sQuery(id+"F5.wireOp",EDGE,"E76.trimOffspring")])],"isStart":true})});
            var sketch = newSketch(context, id + "F18", { "sketchPlane" : qUnion([Q0])});
            skLineSegment(sketch, "E88.0.0", {"start": v(33.28, -19.22) * mm, "end": v(29.05, -16.77) * mm});
            skArc(sketch, "E88.0.1", {"start": v(29.05, -16.77) * mm, "mid": v(0, -33.55) * mm, "end": v(-29.05, -16.77) * mm});
            skLineSegment(sketch, "E88.0.2", {"start": v(-29.05, -16.77) * mm, "end": v(-33.28, -19.22) * mm});
            skArc(sketch, "E88.0.3", {"start": v(-33.28, -19.22) * mm, "mid": v(0, -38.43) * mm, "end": v(33.28, -19.22) * mm});
            skSolve(sketch);
        }
        {
            var Q0;
            Q0 = qSketchRegion(id + "F18", true);
            extrude(context, id + "F19", {"entities" : qUnion([Q0]), "operationType" : NewBodyOperationType.REMOVE, "oppositeDirection" : true, "depth" : 6.6 * mm});
        }
        {
            var Q0;
            Q0=makeQuery(id+"F19.boolean.opBoolean","MERGE",FACE,{"derivedFrom":[makeQuery(id+"F6.boolean.opBoolean","COPY",FACE,{"derivedFrom":makeQuery(id+"F6.opExtrude","SWEPT_FACE",FACE,{"disambiguationData":[OSD([sQuery(id+"F5.wireOp",EDGE,"E71")])]})}),makeQuery(id+"F19.opExtrude","SWEPT_FACE",FACE,{"disambiguationData":[OSD([sQuery(id+"F18.wireOp",EDGE,"E88.0.2")])]})]});
            var sketch = newSketch(context, id + "F20", { "sketchPlane" : qUnion([Q0])});
            skLineSegment(sketch, "E89.0.0", {"start": v(-33.55, 13.8) * mm, "end": v(-33.55, 54.44) * mm});
            skLineSegment(sketch, "E89.0.1", {"start": v(-33.55, 54.44) * mm, "end": v(-58.87, 54.44) * mm});
            skFitSpline(sketch, "E89.0.2", {"points": [v(-87.97, 65.9) * mm, v(-57.41, 64.58) * mm, v(-37.52, 34.31) * mm, v(-37.81, 13.18) * mm]});
            skLineSegment(sketch, "E89.0.3", {"start": v(-37.81, 13.8) * mm, "end": v(-33.55, 13.8) * mm});
            skLineSegment(sketch, "E90", {"start": v(-33.55, 24.65) * mm, "end": v(-39.4, 24.65) * mm});
            skSolve(sketch);
        }
        {
            var Q0;
            {var subQ0=sQuery(id+"F20.wireOp",EDGE,"E89.0.3");Q0=makeQuery(id+"F20.imprint","IMPRINT",FACE,{"disambiguationData":[TD([[makeQuery(id+"F20.imprint","IMPRINT",EDGE,{"derivedFrom":subQ0}),1.0]])]});}
            var Q1;
            Q1=sQuery(id+"F3.wireOp",EDGE,"E17");
            revolve(context, id + "F21", {"operationType" : NewBodyOperationType.REMOVE, "entities" : qUnion([Q0]), "axis" : qUnion([Q1]), "revolveType" : RevolveType.TWO_DIRECTIONS, "angle" : 10 * degree, "angleBack" : 230 * degree});
        }
        {
            var Q0;
            Q0=makeQuery(id+"F19.boolean.opBoolean","MERGE",EDGE,{"derivedFrom":[makeQuery(id+"F6.boolean.opBoolean","COPY",EDGE,{"derivedFrom":makeQuery(id+"F6.opExtrude","SWEPT_EDGE",EDGE,{"disambiguationData":[OSD([sQuery(id+"F5.wireOp",EDGE,"E71"),sQuery(id+"F5.wireOp",EDGE,"E76.trimOffspring")])]})}),makeQuery(id+"F19.opExtrude","SWEPT_EDGE",EDGE,{"disambiguationData":[OSD([sQuery(id+"F18.wireOp",EDGE,"E88.0.1"),sQuery(id+"F18.wireOp",EDGE,"E88.0.2")])]})]});
            var Q1;
            Q1=makeQuery(id+"F21.boolean.opBoolean","MERGE",EDGE,{"derivedFrom":[makeQuery(id+"F19.boolean.opBoolean","COPY",EDGE,{"derivedFrom":makeQuery(id+"F19.opExtrude","CAP_EDGE",EDGE,{"disambiguationData":[OSD([sQuery(id+"F18.wireOp",EDGE,"E88.0.1")])],"isStart":false})}),makeQuery(id+"F21.opRevolve","SWEPT_EDGE",EDGE,{"disambiguationData":[OSD([sQuery(id+"F20.wireOp",EDGE,"E89.0.0"),sQuery(id+"F20.wireOp",EDGE,"E89.0.3")])]})]});
            var Q2;
            Q2=makeQuery(id+"F19.boolean.opBoolean","MERGE",EDGE,{"derivedFrom":[makeQuery(id+"F6.boolean.opBoolean","COPY",EDGE,{"derivedFrom":makeQuery(id+"F6.opExtrude","SWEPT_EDGE",EDGE,{"disambiguationData":[OSD([sQuery(id+"F5.wireOp",EDGE,"E72"),sQuery(id+"F5.wireOp",EDGE,"E76.trimOffspring")])]})}),makeQuery(id+"F19.opExtrude","SWEPT_EDGE",EDGE,{"disambiguationData":[OSD([sQuery(id+"F18.wireOp",EDGE,"E88.0.0"),sQuery(id+"F18.wireOp",EDGE,"E88.0.1")])]})]});
            var Q3;
            {var subQ0=sQuery(id+"F20.wireOp",EDGE,"E89.0.0");var subQ1=sQuery(id+"F20.wireOp",EDGE,"E90");Q3=makeQuery(id+"F21.boolean.opBoolean","COPY",EDGE,{"disambiguationData":[TD([makeQuery(id+"F6.boolean.opBoolean","COPY",FACE,{"derivedFrom":makeQuery(id+"F6.opExtrude","SWEPT_FACE",FACE,{"disambiguationData":[OSD([sQuery(id+"F5.wireOp",EDGE,"E72")])]})})])],"derivedFrom":makeQuery(id+"F21.opRevolve","SWEPT_EDGE",EDGE,{"disambiguationData":[OSD([subQ0,subQ1])]})});}
            var Q4;
            Q4=makeQuery(id+"F21.boolean.opBoolean","COPY",EDGE,{"derivedFrom":makeQuery(id+"F21.opRevolve","CAP_EDGE",EDGE,{"disambiguationData":[OSD([sQuery(id+"F20.wireOp",EDGE,"E89.0.0")])],"isStart":false})});
            var Q5;
            {var subQ0=sQuery(id+"F20.wireOp",EDGE,"E89.0.0");var subQ1=sQuery(id+"F20.wireOp",EDGE,"E90");Q5=makeQuery(id+"F21.boolean.opBoolean","COPY",EDGE,{"disambiguationData":[TD([makeQuery(id+"F6.boolean.opBoolean","COPY",FACE,{"derivedFrom":makeQuery(id+"F6.opExtrude","SWEPT_FACE",FACE,{"disambiguationData":[OSD([sQuery(id+"F5.wireOp",EDGE,"E71")])]})})])],"derivedFrom":makeQuery(id+"F21.opRevolve","SWEPT_EDGE",EDGE,{"disambiguationData":[OSD([subQ0,subQ1])]})});}
            var Q6;
            Q6=makeQuery(id+"F21.boolean.opBoolean","COPY",EDGE,{"derivedFrom":makeQuery(id+"F21.opRevolve","CAP_EDGE",EDGE,{"disambiguationData":[OSD([sQuery(id+"F20.wireOp",EDGE,"E89.0.0")])],"isStart":true})});
            fillet(context, id + "F22", {"entities" : qUnion([Q0, Q1, Q2, Q3, Q4, Q5, Q6]), "radius" : 5 * mm, "tangentPropagation" : true, "allowEdgeOverflow" : false});
        }
        {
            var Q0;
            Q0=makeQuery(id+"F6.boolean.opBoolean","COPY",FACE,{"derivedFrom":makeQuery(id+"F6.opExtrude","CAP_FACE",FACE,{"disambiguationData":[OSD([sQuery(id+"F5.wireOp",EDGE,"E62"),sQuery(id+"F5.wireOp",EDGE,"E63"),sQuery(id+"F5.wireOp",EDGE,"E64.trimOffspring"),sQuery(id+"F5.wireOp",EDGE,"E65.MirrorCS"),sQuery(id+"F5.wireOp",EDGE,"E66.MirrorCS"),sQuery(id+"F5.wireOp",EDGE,"E67.MirrorCS")])],"isStart":false})});
            cPlane(context, id + "F23", {"entities" : qUnion([Q0]), "cplaneType" : CPlaneType.OFFSET, "offset" : 0 * mm, "width" : 150 * mm, "height" : 150 * mm});
        }
        {
            var Q0;
            Q0=qCreatedBy(id+"F23.planeOp",FACE);
            var sketch = newSketch(context, id + "F24", { "sketchPlane" : qUnion([Q0])});
            skCircle(sketch, "E91.0", {"center": v(-64.95, 37.5) * mm, "radius": 4 * mm});
            skCircle(sketch, "E92.0", {"center": v(-64.95, -37.5) * mm, "radius": 4 * mm});
            skCircle(sketch, "E93.0", {"center": v(0, -75) * mm, "radius": 4 * mm});
            skCircle(sketch, "E94.0", {"center": v(64.95, -37.5) * mm, "radius": 4 * mm});
            skCircle(sketch, "E95.0", {"center": v(64.95, 37.5) * mm, "radius": 4 * mm});
            skCircle(sketch, "E96", {"center": v(-64.95, 37.5) * mm, "radius": 6.4 * mm});
            skCircle(sketch, "E97", {"center": v(-64.95, -37.5) * mm, "radius": 6.4 * mm});
            skCircle(sketch, "E98", {"center": v(0, -75) * mm, "radius": 6.4 * mm});
            skCircle(sketch, "E99", {"center": v(64.95, -37.5) * mm, "radius": 6.4 * mm});
            skCircle(sketch, "E100", {"center": v(64.95, 37.5) * mm, "radius": 6.4 * mm});
            skSolve(sketch);
        }
        {
            var Q0;
            Q0 = qSketchRegion(id + "F24", true);
            extrude(context, id + "F25", {"entities" : qUnion([Q0]), "operationType" : NewBodyOperationType.REMOVE, "oppositeDirection" : true, "depth" : 3.8 * mm, "hasSecondDirection" : true, "secondDirectionOppositeDirection" : false, "secondDirectionDepth" : 25 * mm});
        }
    });
